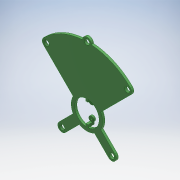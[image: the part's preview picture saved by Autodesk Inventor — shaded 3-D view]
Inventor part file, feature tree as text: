
AUTODESK INVENTOR PART (.ipt)
format: ipt  version: 2018.2 (Build 222227000, 227)  size: 190,976 bytes
history: native  units: mm
features: extrude x3, sketch x2, mirror x1, projected_geometry x1
ambient origin geometry x8: Origin, YZ Plane, XZ Plane, XY Plane, X Axis, Y Axis, Z Axis, Center Point
bodies: Solid1 (feature_tree)
feature tree (7):
  sketch  "Sketch1"  dims[d0=27.9mm d1=2.96mm d2=2.96mm d3=0.15mm d4=0.15mm d5=0.15mm d7=4.0mm]
  extrude  "Extrusion1"  Depth=4.0mm
  extrude  "Extrusion2"  TaperAngle=45.0deg  [1 undecoded]
  extrude  "Extrusion3"  Depth=40.0mm
  mirror  "Mirror1"
  sketch  "Sketch2"  dims[d8=45.0deg d9=45.0deg d10=40.0mm d11=65.0mm d12=6.0mm d13=6.0mm d14=5.0mm d15=5.0mm d17=6.0mm d18=10.0mm d19=2.5mm d20=0.0mm d21=5.0mm d22=0.0mm d23=1.83mm d24=8.465mm d25=2.0mm d26=0.0mm]
  projected_geometry  "Projected Loop1"
note: 1 required parameter value undecoded (feature->parameter linkage not recoverable at this tier; creation-order binding heuristic only, values carry confidence <= 0.55)
